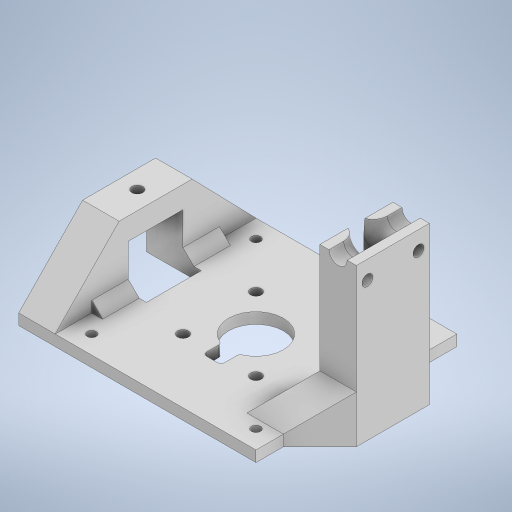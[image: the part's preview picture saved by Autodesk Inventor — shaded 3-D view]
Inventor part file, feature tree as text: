
AUTODESK INVENTOR PART (.ipt)
format: ipt  version: 2023 (Build 270158000, 158)  size: 412,160 bytes
history: native  units: in
note: dims shown in document units (in); Inventor stores cm internally (conversion verified against a paired STEP export)
features: extrude x8, sketch x8, chamfer x5, fillet x1
ambient origin geometry x8: Origin, YZ Plane, XZ Plane, XY Plane, X Axis, Y Axis, Z Axis, Center Point
bodies: Solid1 (feature_tree)
feature tree (22):
  extrude  "Extrusion1"  Depth=1.7717in
  extrude  "Extrusion3"  Depth=0.0984in
  extrude  "Extrusion4"  Depth=0.0984in
  extrude  "Extrusion5"  Depth=0.7874in
  chamfer  "Chamfer5"  Distance=0.1181in
  chamfer  "Chamfer6"  Distance=0.1181in
  extrude  "Extrusion6"  Depth=0.3937in
  extrude  "Extrusion7"  Depth=0.3937in
  extrude  "Extrusion8"  Depth=0.3937in
  extrude  "Extrusion9"  Depth=0.3937in
  fillet  "Fillet1"  Radius=0.1181in
  chamfer  "Chamfer8"  Distance=0.5906in
  chamfer  "Chamfer9"  Distance=0.3937in
  chamfer  "Chamfer10"  Distance=0.3937in
  sketch  "Sketch1"  dims[d0=1.7717in d1=1.7717in]
  sketch  "Sketch3"  dims[d2=0.0984in d3=0.0984in]
  sketch  "Sketch4"  dims[d4=0.0984in d5=0.0984in]
  sketch  "Sketch5"  dims[d6=0.7874in d7=0.7874in]
  sketch  "Sketch6"  dims[d8=0.4921in]
  sketch  "Sketch7"  dims[d9=0.4921in]
  sketch  "Sketch8"  dims[d10=0.1181in]
  sketch  "Sketch9"  dims[d11=0.1181in d12=0.1181in d13=0.1181in d14=2.1654in d15=2.1654in d16=0.1969in d17=0.1969in d22=0.1181in d23=0.0in d24=0.5906in d27=0.3937in d28=0.3937in d29=0.1969in d30=0.1969in d31=0.1969in d32=0.0394in d33=0.2953in d34=0.3937in d35=0.7874in d52=0.3937in d53=0.5906in d54=0.7874in d55=0.2362in d58=0.5906in d59=0.2953in d60=0.3937in d61=0.0in d62=0.1181in d63=0.3937in d64=0.0in d65=0.5906in d66=0.5906in d67=0.0in d68=0.1181in d69=0.0787in d70=45.0deg d71=0.0in d72=0.3937in d73=0.3937in d74=0.1181in d75=0.0787in d76=45.0deg d77=0.3937in d78=0.3937in d79=0.0in d80=1.5748in d81=0.0in d82=0.1969in d83=1.5748in d84=0.0in d85=0.1969in d86=0.1181in d87=0.5512in d88=0.1181in d89=0.1181in d90=0.3937in d91=0.0in d95=0.315in d96=0.1575in d97=0.2953in d98=0.0in d99=0.1575in d100=0.3937in d101=0.0787in d102=45.0deg d103=0.3937in d104=0.0787in d105=45.0deg d106=0.3937in d107=0.0787in d108=45.0deg d38=0.0197in d39=0.0344in d40=0.0197in d41=0.0344in d109=0.0in d110=0.0in d111=0.0in d112=0.0in]
